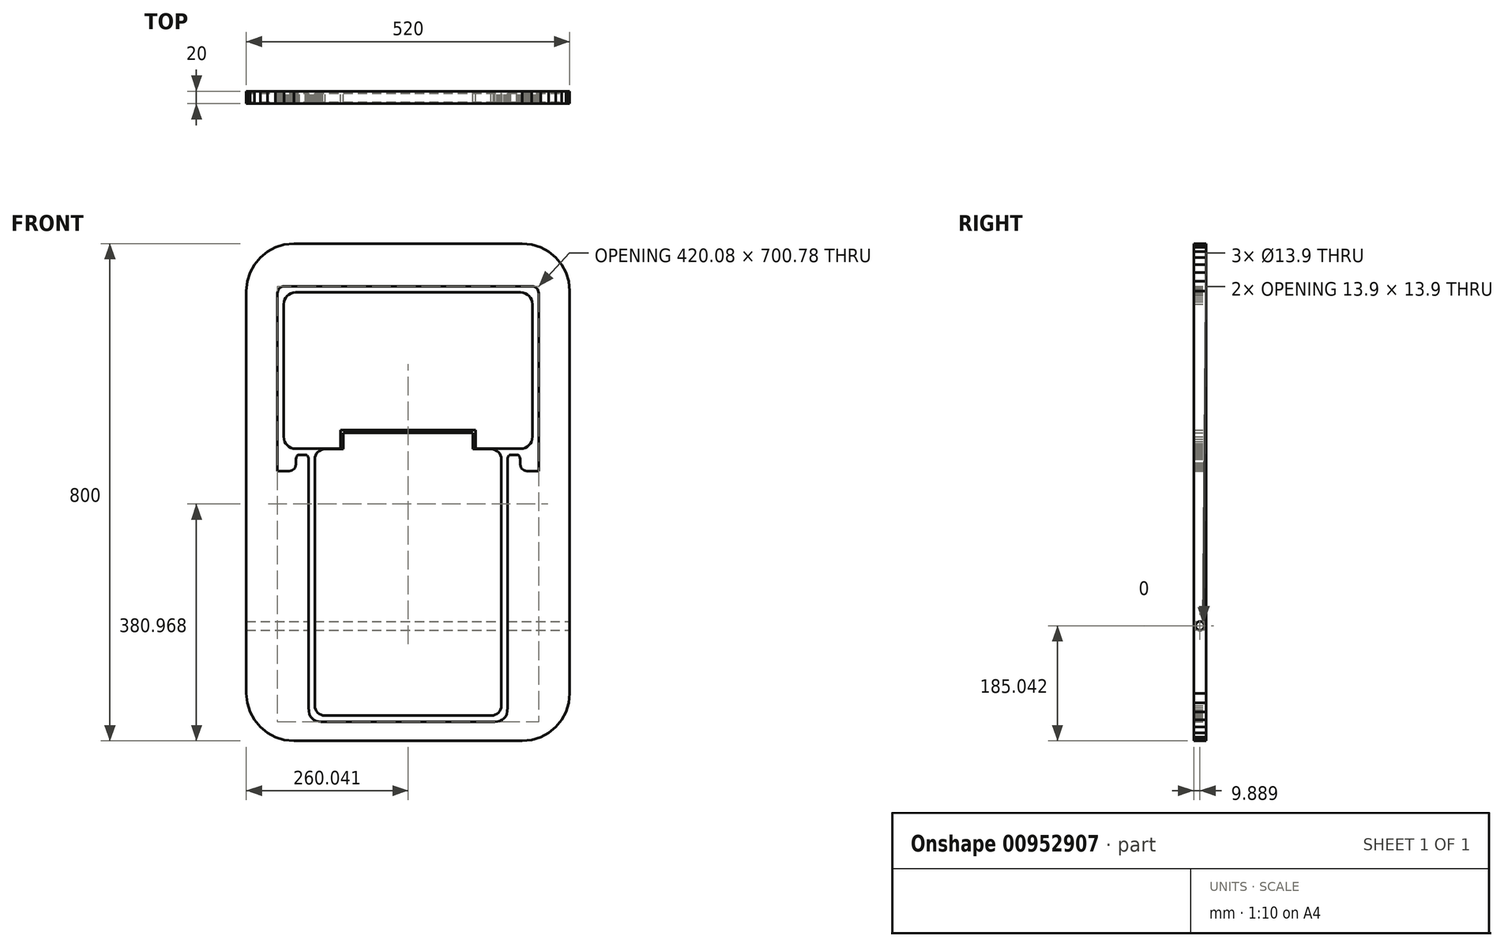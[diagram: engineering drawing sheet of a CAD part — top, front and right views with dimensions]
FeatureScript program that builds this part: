
annotation { "Feature Type Name" : "Feature", "Feature Type Description" : "" }
export const myFeature = defineFeature(function(context is Context, id is Id, definition is map)
    precondition{}
    {
        {
            var Q0;
            Q0=qCreatedBy(makeId("Front.planeOp"),FACE);
            var sketch = newSketch(context, id + "F0", { "sketchPlane" : qUnion([Q0])});
            skLineSegment(sketch, "E0", {"start": v(-183.76, 400) * mm, "end": v(183.76, 400) * mm});
            skLineSegment(sketch, "E1", {"start": v(183.76, 400) * mm, "end": v(199.08, 398.44) * mm});
            skLineSegment(sketch, "E2", {"start": v(199.08, 398.44) * mm, "end": v(213.36, 393.98) * mm});
            skLineSegment(sketch, "E3", {"start": v(213.36, 393.98) * mm, "end": v(226.31, 386.93) * mm});
            skLineSegment(sketch, "E4", {"start": v(226.31, 386.93) * mm, "end": v(237.6, 377.6) * mm});
            skLineSegment(sketch, "E5", {"start": v(237.6, 377.6) * mm, "end": v(246.93, 366.31) * mm});
            skLineSegment(sketch, "E6", {"start": v(246.93, 366.31) * mm, "end": v(253.98, 353.36) * mm});
            skLineSegment(sketch, "E7", {"start": v(253.98, 353.36) * mm, "end": v(258.44, 339.08) * mm});
            skLineSegment(sketch, "E8", {"start": v(258.44, 339.08) * mm, "end": v(260, 323.76) * mm});
            skLineSegment(sketch, "E9", {"start": v(260, 323.76) * mm, "end": v(260, -323.76) * mm});
            skLineSegment(sketch, "E10", {"start": v(260, -323.76) * mm, "end": v(258.44, -339.08) * mm});
            skLineSegment(sketch, "E11", {"start": v(258.44, -339.08) * mm, "end": v(253.98, -353.36) * mm});
            skLineSegment(sketch, "E12", {"start": v(253.98, -353.36) * mm, "end": v(246.93, -366.31) * mm});
            skLineSegment(sketch, "E13", {"start": v(246.93, -366.31) * mm, "end": v(237.6, -377.6) * mm});
            skLineSegment(sketch, "E14", {"start": v(237.6, -377.6) * mm, "end": v(226.31, -386.93) * mm});
            skLineSegment(sketch, "E15", {"start": v(226.31, -386.93) * mm, "end": v(213.36, -393.98) * mm});
            skLineSegment(sketch, "E16", {"start": v(213.36, -393.98) * mm, "end": v(199.08, -398.44) * mm});
            skLineSegment(sketch, "E17", {"start": v(199.08, -398.44) * mm, "end": v(183.76, -400) * mm});
            skLineSegment(sketch, "E18", {"start": v(183.76, -400) * mm, "end": v(-183.76, -400) * mm});
            skLineSegment(sketch, "E19", {"start": v(-183.76, -400) * mm, "end": v(-199.08, -398.44) * mm});
            skLineSegment(sketch, "E20", {"start": v(-199.08, -398.44) * mm, "end": v(-213.36, -393.98) * mm});
            skLineSegment(sketch, "E21", {"start": v(-213.36, -393.98) * mm, "end": v(-226.31, -386.93) * mm});
            skLineSegment(sketch, "E22", {"start": v(-226.31, -386.93) * mm, "end": v(-237.6, -377.6) * mm});
            skLineSegment(sketch, "E23", {"start": v(-237.6, -377.6) * mm, "end": v(-246.93, -366.31) * mm});
            skLineSegment(sketch, "E24", {"start": v(-246.93, -366.31) * mm, "end": v(-253.98, -353.36) * mm});
            skLineSegment(sketch, "E25", {"start": v(-253.98, -353.36) * mm, "end": v(-258.44, -339.08) * mm});
            skLineSegment(sketch, "E26", {"start": v(-258.44, -339.08) * mm, "end": v(-260, -323.76) * mm});
            skLineSegment(sketch, "E27", {"start": v(-260, -323.76) * mm, "end": v(-260, 323.76) * mm});
            skLineSegment(sketch, "E28", {"start": v(-260, 323.76) * mm, "end": v(-258.44, 339.08) * mm});
            skLineSegment(sketch, "E29", {"start": v(-258.44, 339.08) * mm, "end": v(-253.98, 353.36) * mm});
            skLineSegment(sketch, "E30", {"start": v(-253.98, 353.36) * mm, "end": v(-246.93, 366.31) * mm});
            skLineSegment(sketch, "E31", {"start": v(-246.93, 366.31) * mm, "end": v(-237.6, 377.6) * mm});
            skLineSegment(sketch, "E32", {"start": v(-237.6, 377.6) * mm, "end": v(-226.31, 386.93) * mm});
            skLineSegment(sketch, "E33", {"start": v(-226.31, 386.93) * mm, "end": v(-213.36, 393.98) * mm});
            skLineSegment(sketch, "E34", {"start": v(-213.36, 393.98) * mm, "end": v(-199.08, 398.44) * mm});
            skLineSegment(sketch, "E35", {"start": v(-199.08, 398.44) * mm, "end": v(-183.76, 400) * mm});
            skLineSegment(sketch, "E36", {"start": v(140.04, -369.42) * mm, "end": v(144.28, -368.85) * mm});
            skLineSegment(sketch, "E37", {"start": v(144.28, -368.85) * mm, "end": v(148.13, -367.78) * mm});
            skLineSegment(sketch, "E38", {"start": v(148.13, -367.78) * mm, "end": v(151.54, -366.13) * mm});
            skLineSegment(sketch, "E39", {"start": v(151.54, -366.13) * mm, "end": v(154.45, -363.82) * mm});
            skLineSegment(sketch, "E40", {"start": v(154.45, -363.82) * mm, "end": v(156.8, -360.78) * mm});
            skLineSegment(sketch, "E41", {"start": v(156.8, -360.78) * mm, "end": v(158.55, -356.94) * mm});
            skLineSegment(sketch, "E42", {"start": v(158.55, -356.94) * mm, "end": v(159.63, -352.23) * mm});
            skLineSegment(sketch, "E43", {"start": v(159.63, -352.23) * mm, "end": v(160, -346.57) * mm});
            skLineSegment(sketch, "E44", {"start": v(160, -346.57) * mm, "end": v(160.07, -4.19) * mm});
            skLineSegment(sketch, "E45", {"start": v(160.07, -4.19) * mm, "end": v(160.08, 38.4) * mm});
            skLineSegment(sketch, "E46", {"start": v(160.08, 38.4) * mm, "end": v(160.08, 53.56) * mm});
            skLineSegment(sketch, "E47", {"start": v(160.08, 53.56) * mm, "end": v(160.18, 55.05) * mm});
            skLineSegment(sketch, "E48", {"start": v(160.18, 55.05) * mm, "end": v(160.42, 56.36) * mm});
            skLineSegment(sketch, "E49", {"start": v(160.42, 56.36) * mm, "end": v(160.8, 57.47) * mm});
            skLineSegment(sketch, "E50", {"start": v(160.8, 57.47) * mm, "end": v(161.32, 58.4) * mm});
            skLineSegment(sketch, "E51", {"start": v(161.32, 58.4) * mm, "end": v(161.99, 59.1) * mm});
            skLineSegment(sketch, "E52", {"start": v(161.99, 59.1) * mm, "end": v(162.8, 59.62) * mm});
            skLineSegment(sketch, "E53", {"start": v(162.8, 59.62) * mm, "end": v(163.77, 59.92) * mm});
            skLineSegment(sketch, "E54", {"start": v(163.77, 59.92) * mm, "end": v(164.9, 60) * mm});
            skLineSegment(sketch, "E55", {"start": v(164.9, 60) * mm, "end": v(174.51, 60) * mm});
            skLineSegment(sketch, "E56", {"start": v(174.51, 60) * mm, "end": v(175.68, 59.94) * mm});
            skLineSegment(sketch, "E57", {"start": v(175.68, 59.94) * mm, "end": v(176.71, 59.67) * mm});
            skLineSegment(sketch, "E58", {"start": v(176.71, 59.67) * mm, "end": v(177.61, 59.2) * mm});
            skLineSegment(sketch, "E59", {"start": v(177.61, 59.2) * mm, "end": v(178.38, 58.54) * mm});
            skLineSegment(sketch, "E60", {"start": v(178.38, 58.54) * mm, "end": v(179.01, 57.68) * mm});
            skLineSegment(sketch, "E61", {"start": v(179.01, 57.68) * mm, "end": v(179.52, 56.62) * mm});
            skLineSegment(sketch, "E62", {"start": v(179.52, 56.62) * mm, "end": v(179.89, 55.37) * mm});
            skLineSegment(sketch, "E63", {"start": v(179.89, 55.37) * mm, "end": v(180.13, 53.91) * mm});
            skLineSegment(sketch, "E64", {"start": v(180.13, 53.91) * mm, "end": v(180.1, 47.03) * mm});
            skLineSegment(sketch, "E65", {"start": v(180.1, 47.03) * mm, "end": v(180.27, 44.45) * mm});
            skLineSegment(sketch, "E66", {"start": v(180.27, 44.45) * mm, "end": v(180.83, 42.03) * mm});
            skLineSegment(sketch, "E67", {"start": v(180.83, 42.03) * mm, "end": v(181.74, 39.83) * mm});
            skLineSegment(sketch, "E68", {"start": v(181.74, 39.83) * mm, "end": v(183.01, 37.9) * mm});
            skLineSegment(sketch, "E69", {"start": v(183.01, 37.9) * mm, "end": v(184.63, 36.31) * mm});
            skLineSegment(sketch, "E70", {"start": v(184.63, 36.31) * mm, "end": v(186.58, 35.1) * mm});
            skLineSegment(sketch, "E71", {"start": v(186.58, 35.1) * mm, "end": v(188.86, 34.34) * mm});
            skLineSegment(sketch, "E72", {"start": v(188.86, 34.34) * mm, "end": v(191.45, 34.07) * mm});
            skLineSegment(sketch, "E73", {"start": v(191.45, 34.07) * mm, "end": v(210.07, 34.06) * mm});
            skLineSegment(sketch, "E74", {"start": v(210.07, 34.06) * mm, "end": v(210.08, 63.97) * mm});
            skLineSegment(sketch, "E75", {"start": v(210.08, 63.97) * mm, "end": v(210.08, 320.26) * mm});
            skLineSegment(sketch, "E76", {"start": v(210.08, 320.26) * mm, "end": v(209.85, 322.49) * mm});
            skLineSegment(sketch, "E77", {"start": v(209.85, 322.49) * mm, "end": v(209.2, 324.57) * mm});
            skLineSegment(sketch, "E78", {"start": v(209.2, 324.57) * mm, "end": v(208.18, 326.45) * mm});
            skLineSegment(sketch, "E79", {"start": v(208.18, 326.45) * mm, "end": v(206.82, 328.1) * mm});
            skLineSegment(sketch, "E80", {"start": v(206.82, 328.1) * mm, "end": v(205.17, 329.45) * mm});
            skLineSegment(sketch, "E81", {"start": v(205.17, 329.45) * mm, "end": v(203.28, 330.48) * mm});
            skLineSegment(sketch, "E82", {"start": v(203.28, 330.48) * mm, "end": v(201.19, 331.13) * mm});
            skLineSegment(sketch, "E83", {"start": v(201.19, 331.13) * mm, "end": v(198.94, 331.36) * mm});
            skLineSegment(sketch, "E84", {"start": v(198.94, 331.36) * mm, "end": v(-198.9, 331.36) * mm});
            skLineSegment(sketch, "E85", {"start": v(-198.9, 331.36) * mm, "end": v(-201.13, 331.13) * mm});
            skLineSegment(sketch, "E86", {"start": v(-201.13, 331.13) * mm, "end": v(-203.21, 330.48) * mm});
            skLineSegment(sketch, "E87", {"start": v(-203.21, 330.48) * mm, "end": v(-205.1, 329.45) * mm});
            skLineSegment(sketch, "E88", {"start": v(-205.1, 329.45) * mm, "end": v(-206.74, 328.1) * mm});
            skLineSegment(sketch, "E89", {"start": v(-206.74, 328.1) * mm, "end": v(-208.1, 326.45) * mm});
            skLineSegment(sketch, "E90", {"start": v(-208.1, 326.45) * mm, "end": v(-209.12, 324.57) * mm});
            skLineSegment(sketch, "E91", {"start": v(-209.12, 324.57) * mm, "end": v(-209.77, 322.49) * mm});
            skLineSegment(sketch, "E92", {"start": v(-209.77, 322.49) * mm, "end": v(-210, 320.26) * mm});
            skLineSegment(sketch, "E93", {"start": v(-210, 320.26) * mm, "end": v(-210, 63.97) * mm});
            skLineSegment(sketch, "E94", {"start": v(-210, 63.97) * mm, "end": v(-210, 34.06) * mm});
            skLineSegment(sketch, "E95", {"start": v(-210, 34.06) * mm, "end": v(-191.36, 34.07) * mm});
            skLineSegment(sketch, "E96", {"start": v(-191.36, 34.07) * mm, "end": v(-188.77, 34.34) * mm});
            skLineSegment(sketch, "E97", {"start": v(-188.77, 34.34) * mm, "end": v(-186.5, 35.1) * mm});
            skLineSegment(sketch, "E98", {"start": v(-186.5, 35.1) * mm, "end": v(-184.55, 36.31) * mm});
            skLineSegment(sketch, "E99", {"start": v(-184.55, 36.31) * mm, "end": v(-182.93, 37.9) * mm});
            skLineSegment(sketch, "E100", {"start": v(-182.93, 37.9) * mm, "end": v(-181.66, 39.83) * mm});
            skLineSegment(sketch, "E101", {"start": v(-181.66, 39.83) * mm, "end": v(-180.74, 42.03) * mm});
            skLineSegment(sketch, "E102", {"start": v(-180.74, 42.03) * mm, "end": v(-180.2, 44.45) * mm});
            skLineSegment(sketch, "E103", {"start": v(-180.2, 44.45) * mm, "end": v(-180.01, 47.03) * mm});
            skLineSegment(sketch, "E104", {"start": v(-180.01, 47.03) * mm, "end": v(-180.05, 53.91) * mm});
            skLineSegment(sketch, "E105", {"start": v(-180.05, 53.91) * mm, "end": v(-179.8, 55.37) * mm});
            skLineSegment(sketch, "E106", {"start": v(-179.8, 55.37) * mm, "end": v(-179.43, 56.62) * mm});
            skLineSegment(sketch, "E107", {"start": v(-179.43, 56.62) * mm, "end": v(-178.93, 57.68) * mm});
            skLineSegment(sketch, "E108", {"start": v(-178.93, 57.68) * mm, "end": v(-178.3, 58.54) * mm});
            skLineSegment(sketch, "E109", {"start": v(-178.3, 58.54) * mm, "end": v(-177.53, 59.2) * mm});
            skLineSegment(sketch, "E110", {"start": v(-177.53, 59.2) * mm, "end": v(-176.63, 59.67) * mm});
            skLineSegment(sketch, "E111", {"start": v(-176.63, 59.67) * mm, "end": v(-175.6, 59.94) * mm});
            skLineSegment(sketch, "E112", {"start": v(-175.6, 59.94) * mm, "end": v(-174.43, 60) * mm});
            skLineSegment(sketch, "E113", {"start": v(-174.43, 60) * mm, "end": v(-164.82, 60) * mm});
            skLineSegment(sketch, "E114", {"start": v(-164.82, 60) * mm, "end": v(-163.7, 59.92) * mm});
            skLineSegment(sketch, "E115", {"start": v(-163.7, 59.92) * mm, "end": v(-162.72, 59.62) * mm});
            skLineSegment(sketch, "E116", {"start": v(-162.72, 59.62) * mm, "end": v(-161.9, 59.1) * mm});
            skLineSegment(sketch, "E117", {"start": v(-161.9, 59.1) * mm, "end": v(-161.24, 58.4) * mm});
            skLineSegment(sketch, "E118", {"start": v(-161.24, 58.4) * mm, "end": v(-160.72, 57.47) * mm});
            skLineSegment(sketch, "E119", {"start": v(-160.72, 57.47) * mm, "end": v(-160.34, 56.36) * mm});
            skLineSegment(sketch, "E120", {"start": v(-160.34, 56.36) * mm, "end": v(-160.1, 55.05) * mm});
            skLineSegment(sketch, "E121", {"start": v(-160.1, 55.05) * mm, "end": v(-160, 53.56) * mm});
            skLineSegment(sketch, "E122", {"start": v(-160, 53.56) * mm, "end": v(-160, 38.4) * mm});
            skLineSegment(sketch, "E123", {"start": v(-160, 38.4) * mm, "end": v(-159.99, -4.19) * mm});
            skLineSegment(sketch, "E124", {"start": v(-159.99, -4.19) * mm, "end": v(-159.92, -346.57) * mm});
            skLineSegment(sketch, "E125", {"start": v(-159.92, -346.57) * mm, "end": v(-159.55, -352.23) * mm});
            skLineSegment(sketch, "E126", {"start": v(-159.55, -352.23) * mm, "end": v(-158.47, -356.94) * mm});
            skLineSegment(sketch, "E127", {"start": v(-158.47, -356.94) * mm, "end": v(-156.72, -360.78) * mm});
            skLineSegment(sketch, "E128", {"start": v(-156.72, -360.78) * mm, "end": v(-154.37, -363.82) * mm});
            skLineSegment(sketch, "E129", {"start": v(-154.37, -363.82) * mm, "end": v(-151.47, -366.13) * mm});
            skLineSegment(sketch, "E130", {"start": v(-151.47, -366.13) * mm, "end": v(-148.07, -367.78) * mm});
            skLineSegment(sketch, "E131", {"start": v(-148.07, -367.78) * mm, "end": v(-144.22, -368.85) * mm});
            skLineSegment(sketch, "E132", {"start": v(-144.22, -368.85) * mm, "end": v(-140, -369.42) * mm});
            skLineSegment(sketch, "E133", {"start": v(-140, -369.42) * mm, "end": v(140.04, -369.42) * mm});
            skLineSegment(sketch, "E134", {"start": v(-180.97, 321.36) * mm, "end": v(181.05, 321.36) * mm});
            skLineSegment(sketch, "E135", {"start": v(181.05, 321.36) * mm, "end": v(184.87, 320.97) * mm});
            skLineSegment(sketch, "E136", {"start": v(184.87, 320.97) * mm, "end": v(188.44, 319.85) * mm});
            skLineSegment(sketch, "E137", {"start": v(188.44, 319.85) * mm, "end": v(191.67, 318.1) * mm});
            skLineSegment(sketch, "E138", {"start": v(191.67, 318.1) * mm, "end": v(194.5, 315.77) * mm});
            skLineSegment(sketch, "E139", {"start": v(194.5, 315.77) * mm, "end": v(196.82, 312.95) * mm});
            skLineSegment(sketch, "E140", {"start": v(196.82, 312.95) * mm, "end": v(198.58, 309.72) * mm});
            skLineSegment(sketch, "E141", {"start": v(198.58, 309.72) * mm, "end": v(199.7, 306.15) * mm});
            skLineSegment(sketch, "E142", {"start": v(199.7, 306.15) * mm, "end": v(200.08, 302.33) * mm});
            skLineSegment(sketch, "E143", {"start": v(200.08, 302.33) * mm, "end": v(200.08, 89.03) * mm});
            skLineSegment(sketch, "E144", {"start": v(200.08, 89.03) * mm, "end": v(199.7, 85.2) * mm});
            skLineSegment(sketch, "E145", {"start": v(199.7, 85.2) * mm, "end": v(198.58, 81.64) * mm});
            skLineSegment(sketch, "E146", {"start": v(198.58, 81.64) * mm, "end": v(196.82, 78.4) * mm});
            skLineSegment(sketch, "E147", {"start": v(196.82, 78.4) * mm, "end": v(194.5, 75.59) * mm});
            skLineSegment(sketch, "E148", {"start": v(194.5, 75.59) * mm, "end": v(191.67, 73.26) * mm});
            skLineSegment(sketch, "E149", {"start": v(191.67, 73.26) * mm, "end": v(188.44, 71.5) * mm});
            skLineSegment(sketch, "E150", {"start": v(188.44, 71.5) * mm, "end": v(184.87, 70.39) * mm});
            skLineSegment(sketch, "E151", {"start": v(184.87, 70.39) * mm, "end": v(181.05, 70) * mm});
            skLineSegment(sketch, "E152", {"start": v(181.05, 70) * mm, "end": v(108.76, 70) * mm});
            skLineSegment(sketch, "E153", {"start": v(-180.97, 70) * mm, "end": v(-184.8, 70.39) * mm});
            skLineSegment(sketch, "E154", {"start": v(-184.8, 70.39) * mm, "end": v(-188.36, 71.5) * mm});
            skLineSegment(sketch, "E155", {"start": v(-188.36, 71.5) * mm, "end": v(-191.6, 73.26) * mm});
            skLineSegment(sketch, "E156", {"start": v(-191.6, 73.26) * mm, "end": v(-194.41, 75.59) * mm});
            skLineSegment(sketch, "E157", {"start": v(-194.41, 75.59) * mm, "end": v(-196.74, 78.4) * mm});
            skLineSegment(sketch, "E158", {"start": v(-196.74, 78.4) * mm, "end": v(-198.5, 81.64) * mm});
            skLineSegment(sketch, "E159", {"start": v(-198.5, 81.64) * mm, "end": v(-199.61, 85.2) * mm});
            skLineSegment(sketch, "E160", {"start": v(-199.61, 85.2) * mm, "end": v(-200, 89.03) * mm});
            skLineSegment(sketch, "E161", {"start": v(-200, 89.03) * mm, "end": v(-200, 302.33) * mm});
            skLineSegment(sketch, "E162", {"start": v(-200, 302.33) * mm, "end": v(-199.61, 306.15) * mm});
            skLineSegment(sketch, "E163", {"start": v(-199.61, 306.15) * mm, "end": v(-198.5, 309.72) * mm});
            skLineSegment(sketch, "E164", {"start": v(-198.5, 309.72) * mm, "end": v(-196.74, 312.95) * mm});
            skLineSegment(sketch, "E165", {"start": v(-196.74, 312.95) * mm, "end": v(-194.41, 315.77) * mm});
            skLineSegment(sketch, "E166", {"start": v(-194.41, 315.77) * mm, "end": v(-191.6, 318.1) * mm});
            skLineSegment(sketch, "E167", {"start": v(-191.6, 318.1) * mm, "end": v(-188.36, 319.85) * mm});
            skLineSegment(sketch, "E168", {"start": v(-188.36, 319.85) * mm, "end": v(-184.8, 320.97) * mm});
            skLineSegment(sketch, "E169", {"start": v(-184.8, 320.97) * mm, "end": v(-180.97, 321.36) * mm});
            skLineSegment(sketch, "E170", {"start": v(-133.56, 69.44) * mm, "end": v(-104.24, 69.44) * mm});
            skLineSegment(sketch, "E171", {"start": v(133.67, 69.44) * mm, "end": v(136.95, 69.1) * mm});
            skLineSegment(sketch, "E172", {"start": v(136.95, 69.1) * mm, "end": v(140, 68.15) * mm});
            skLineSegment(sketch, "E173", {"start": v(140, 68.15) * mm, "end": v(142.78, 66.64) * mm});
            skLineSegment(sketch, "E174", {"start": v(142.78, 66.64) * mm, "end": v(145.2, 64.64) * mm});
            skLineSegment(sketch, "E175", {"start": v(145.2, 64.64) * mm, "end": v(147.2, 62.22) * mm});
            skLineSegment(sketch, "E176", {"start": v(147.2, 62.22) * mm, "end": v(148.7, 59.45) * mm});
            skLineSegment(sketch, "E177", {"start": v(148.7, 59.45) * mm, "end": v(149.66, 56.39) * mm});
            skLineSegment(sketch, "E178", {"start": v(149.66, 56.39) * mm, "end": v(150, 53.1) * mm});
            skLineSegment(sketch, "E179", {"start": v(150, 53.1) * mm, "end": v(150, -343.09) * mm});
            skLineSegment(sketch, "E180", {"start": v(150, -343.09) * mm, "end": v(149.66, -346.37) * mm});
            skLineSegment(sketch, "E181", {"start": v(149.66, -346.37) * mm, "end": v(148.7, -349.43) * mm});
            skLineSegment(sketch, "E182", {"start": v(148.7, -349.43) * mm, "end": v(147.2, -352.2) * mm});
            skLineSegment(sketch, "E183", {"start": v(147.2, -352.2) * mm, "end": v(145.2, -354.62) * mm});
            skLineSegment(sketch, "E184", {"start": v(145.2, -354.62) * mm, "end": v(142.78, -356.62) * mm});
            skLineSegment(sketch, "E185", {"start": v(142.78, -356.62) * mm, "end": v(140, -358.13) * mm});
            skLineSegment(sketch, "E186", {"start": v(140, -358.13) * mm, "end": v(136.95, -359.09) * mm});
            skLineSegment(sketch, "E187", {"start": v(136.95, -359.09) * mm, "end": v(133.67, -359.42) * mm});
            skLineSegment(sketch, "E188", {"start": v(133.67, -359.42) * mm, "end": v(-133.56, -359.42) * mm});
            skLineSegment(sketch, "E189", {"start": v(-133.56, -359.42) * mm, "end": v(-136.84, -359.09) * mm});
            skLineSegment(sketch, "E190", {"start": v(-136.84, -359.09) * mm, "end": v(-139.9, -358.13) * mm});
            skLineSegment(sketch, "E191", {"start": v(-139.9, -358.13) * mm, "end": v(-142.68, -356.62) * mm});
            skLineSegment(sketch, "E192", {"start": v(-142.68, -356.62) * mm, "end": v(-145.1, -354.62) * mm});
            skLineSegment(sketch, "E193", {"start": v(-145.1, -354.62) * mm, "end": v(-147.1, -352.2) * mm});
            skLineSegment(sketch, "E194", {"start": v(-147.1, -352.2) * mm, "end": v(-148.6, -349.43) * mm});
            skLineSegment(sketch, "E195", {"start": v(-148.6, -349.43) * mm, "end": v(-149.56, -346.37) * mm});
            skLineSegment(sketch, "E196", {"start": v(-149.56, -346.37) * mm, "end": v(-149.9, -343.09) * mm});
            skLineSegment(sketch, "E197", {"start": v(-149.9, -343.09) * mm, "end": v(-149.9, 53.1) * mm});
            skLineSegment(sketch, "E198", {"start": v(-149.9, 53.1) * mm, "end": v(-149.56, 56.39) * mm});
            skLineSegment(sketch, "E199", {"start": v(-149.56, 56.39) * mm, "end": v(-148.6, 59.45) * mm});
            skLineSegment(sketch, "E200", {"start": v(-148.6, 59.45) * mm, "end": v(-147.1, 62.22) * mm});
            skLineSegment(sketch, "E201", {"start": v(-147.1, 62.22) * mm, "end": v(-145.1, 64.64) * mm});
            skLineSegment(sketch, "E202", {"start": v(-145.1, 64.64) * mm, "end": v(-142.68, 66.64) * mm});
            skLineSegment(sketch, "E203", {"start": v(-142.68, 66.64) * mm, "end": v(-139.9, 68.15) * mm});
            skLineSegment(sketch, "E204", {"start": v(-139.9, 68.15) * mm, "end": v(-136.84, 69.1) * mm});
            skLineSegment(sketch, "E205", {"start": v(-136.84, 69.1) * mm, "end": v(-133.56, 69.44) * mm});
            skLineSegment(sketch, "E206.bottom", {"start": v(108.76, 100.16) * mm, "end": v(-108.76, 100.16) * mm});
            skLineSegment(sketch, "E206.left", {"start": v(108.76, 100.16) * mm, "end": v(108.76, 70) * mm});
            skLineSegment(sketch, "E206.right", {"start": v(-108.76, 100.16) * mm, "end": v(-108.76, 70) * mm});
            skPoint(sketch, "E206.middle", {"position": v(0, 0) * mm});
            skPoint(sketch, "E206.top.end.orphan", {"position": v(-108.76, -100.16) * mm});
            skPoint(sketch, "E207.orphan", {"position": v(108.76, -100.16) * mm});
            skLineSegment(sketch, "E208.trimOffspring", {"start": v(-108.76, 70) * mm, "end": v(-180.97, 70) * mm});
            skLineSegment(sketch, "E209.bottom", {"start": v(-104.24, 95.24) * mm, "end": v(104.34, 95.24) * mm});
            skLineSegment(sketch, "E209.left", {"start": v(-104.24, 95.24) * mm, "end": v(-104.24, 69.44) * mm});
            skLineSegment(sketch, "E209.right", {"start": v(104.34, 95.24) * mm, "end": v(104.34, 69.44) * mm});
            skLineSegment(sketch, "E210.trimOffspring", {"start": v(104.34, 69.44) * mm, "end": v(133.67, 69.44) * mm});
            skSolve(sketch);
        }
        {
            var Q0;
            Q0=makeQuery(id+"F0.imprint","IMPRINT",FACE,{"disambiguationData":[TD([[makeQuery(id+"F0.imprint","IMPRINT",EDGE,{"derivedFrom":sQuery(id+"F0.wireOp",EDGE,"E134")}),-1.0]])]});
            var Q1;
            Q1=makeQuery(id+"F0.imprint","IMPRINT",FACE,{"disambiguationData":[TD([[makeQuery(id+"F0.imprint","IMPRINT",EDGE,{"derivedFrom":sQuery(id+"F0.wireOp",EDGE,"E170")}),-1.0]])]});
            var Q2;
            Q2=makeQuery(id+"F0.imprint","IMPRINT",FACE,{"disambiguationData":[TD([[makeQuery(id+"F0.imprint","IMPRINT",EDGE,{"derivedFrom":sQuery(id+"F0.wireOp",EDGE,"E0")}),-1.0]])]});
            extrude(context, id + "F1", {"entities" : qUnion([Q0, Q1, Q2]), "depth" : 20 * mm, "offsetDistance" : 25 * mm});
        }
        {
            var Q0;
            Q0=qCreatedBy(makeId("Right.planeOp"),FACE);
            var sketch = newSketch(context, id + "F2", { "sketchPlane" : qUnion([Q0])});
            skCircle(sketch, "E211", {"center": v(-10.11, -214.96) * mm, "radius": 6.95 * mm});
            skSolve(sketch);
        }
        {
            var Q0;
            Q0 = qSketchRegion(id + "F2", true);
            extrude(context, id + "F3", {"entities" : qUnion([Q0]), "operationType" : NewBodyOperationType.REMOVE, "endBound" : BoundingType.SYMMETRIC, "oppositeDirection" : true, "depth" : 996 * mm, "offsetDistance" : 25 * mm});
        }
    });
